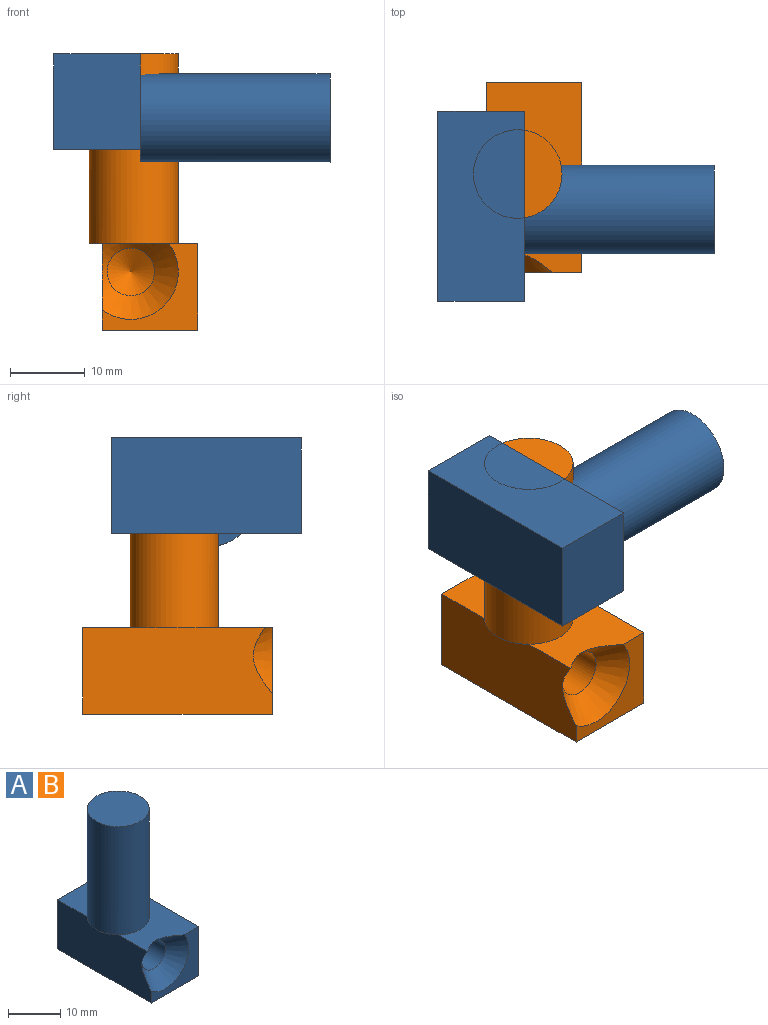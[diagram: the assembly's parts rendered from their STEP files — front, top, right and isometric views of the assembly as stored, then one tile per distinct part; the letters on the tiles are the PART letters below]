
ASSEMBLY  parts=2 mates=1
PART A: 12 faces, bbox 15.3x25.4x36.9 mm
  f0: plane 25.4x12.78mm, normal (0,0,1), area 208mm2, adj f1,f2,f4,f5,f6,f10
  f1: plane 25.4x11.55mm, normal (-1,0,0), area 277.6mm2, adj f0,f2,f3,f5,f8,f10
  f2: plane 12.77x11.55mm, normal (0,-1,0), area 56.5mm2, adj f0,f1,f3,f4,f10
  f3: plane 25.4x12.77mm, normal (0,0,-1), area 324.4mm2, adj f1,f2,f4,f5
  f4: plane 25.4x11.55mm, normal (1,0,0), area 293.3mm2, adj f0,f2,f3,f5
  f5: plane 12.77x11.55mm, normal (0,1,0), area 147.5mm2, adj f0,f1,f3,f4
  f6: cylinder r=5.93mm len=25.4mm, axis (0,0,-1), area 946.4mm2, adj f0,f7,f8
  f7: plane 11.86x11.86mm, normal (0,0,1), area 110.5mm2, adj f6
  f8: plane 8.4x1.75mm, normal (0,0,-1), area 10.1mm2, adj f1,f6
  f9: cylinder r=3.17mm len=9.53mm, axis (0,-1,0), area 190mm2, adj f10,f11
  f10: cone r=3.17mm half-angle=45deg, axis (0,-1,0), area 83.9mm2, adj f0,f1,f2,f9
  f11: cone r=0mm half-angle=59deg, axis (0,-1,0), area 36.9mm2, adj f9
PART B: same geometry as A
PLACE A rot(axis=(0.71,0,0.71),180deg) t=(-26.01,-14.2,-15.08)mm
PLACE B t=(-19.52,15.09,-39.25)mm
MATE planar A.f4 <-> B.f6  axis (0,0,1) through (-20.24,-1.5,-2.3)mm
